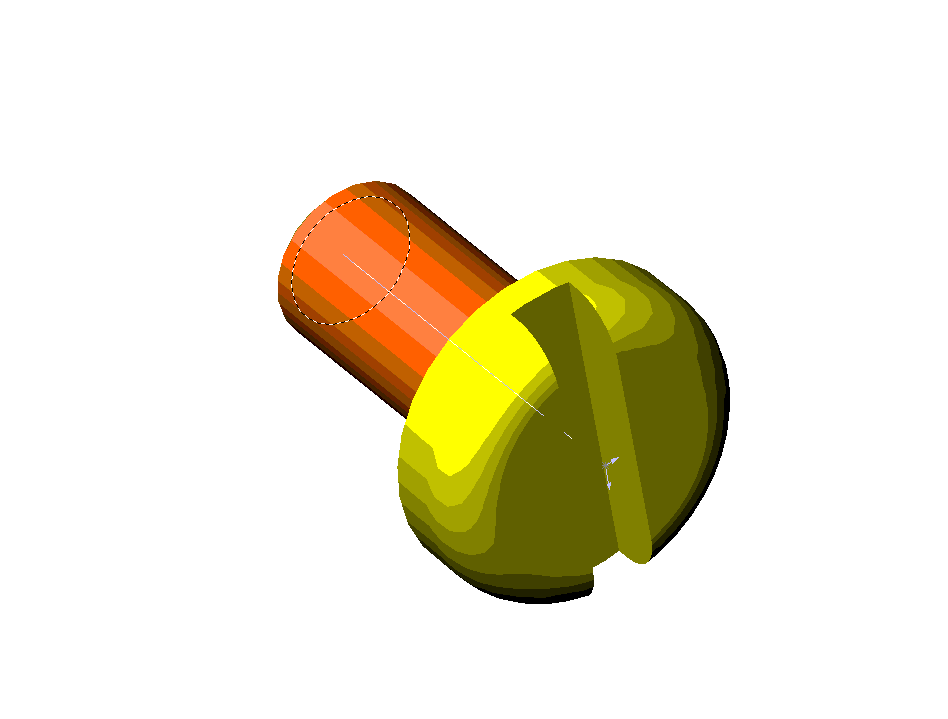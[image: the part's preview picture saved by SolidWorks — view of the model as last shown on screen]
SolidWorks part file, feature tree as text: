
SOLIDWORKS PART (.sldprt)
format: sldprt  version: not decoded by parser v0  size: 114,688 bytes
history: native  units: mm
features: plane x3, sketch x3, extrude x2, material x1, fillet x1, thread x1, chamfer x1, cut_extrude x1 (+10 scaffold rows collapsed)
feature tree (23):
  scaffold x10  (default folders/planes/origin — collapsed)
  material  "Matériau <non spécifié>"
  plane  "Plan1"
  plane  "Plan2"
  plane  "Plan3"
  sketch  "Esquisse1"  dims[D1=5.0mm]
  extrude  "Base-Extrusion"  Depth=1.5mm
  fillet  "Congé1"  Radius=0.8mm
  sketch  "Esquisse2"  dims[D1=2.5mm]
  extrude  "Boss.-Extru.1"  [1 undecoded]
  thread  "Représentation de filetage1"  [2 undecoded]
  chamfer  "Chanfrein1"  Distance=0.2mm Angle=45deg
  sketch  "Esquisse3"  dims[D1=1.0mm D2=1.0mm]
  cut_extrude  "Enlèv. mat.-Extru.1"  [1 undecoded]
decode coverage: 6 of 9 modeling features carry decoded parameters
note: 4 parameter values undecoded
summary: no parameter record found for 3 features
note: suppression state not decoded; provenance and decode notes live in map.json
